# Revit family: FP-Revit20-en-CG301DNGGB5-CG301DNGGG5-GasCooktop-xxxxxxx-xx
name_source: partatom
category: Generic Models
units: mm (PartAtom-declared; Revit-internal decimal feet)

## family parameters
Always vertical = No
Can host rebar = No
Cut with Voids When Loaded = No
Part Type = Normal
Room Calculation Point = No
Round Connector Dimension = Use Diameter
Shared = No
Work Plane-Based = Yes

## types (2) — shared parameters
Chassis - Depth = 484 mm  [stored 1.58793 ft]
Chassis - Height = 61 mm  [stored 0.200131 ft]
Chassis - Width = 256 mm  [stored 0.839895 ft]
Clearance - Combustible = Fisher & Paykel - Clearance Required (Combustible)
Clearance - Non-Combustible = Fisher & Paykel - Clearance Required (Non-Combustible)
Clearance - Overhead Combustible = 650 mm  [stored 2.13255 ft]
Clearance - Overhead Exhaust Fan = 800 mm  [stored 2.62467 ft]
Clearance - Overhead Non-Combustible = 500 mm  [stored 1.64042 ft]
Clearance - Overhead Rangehood = Fisher & Paykel - Clearance Required (Rangehood)
Clearance - Rear Combustible = 85 mm  [stored 0.278871 ft]
Clearance - Side Combustible = 120 mm  [stored 0.393701 ft]
Default Elevation = 1219 mm
Description = Gas on Glass Modular Cooktop, 30cm
Manufacturer = Fisher & Paykel Appliances
Product - Depth = 530 mm  [stored 1.73885 ft]
Product - Height = 127 mm  [stored 0.416667 ft]
Product - Width = 300 mm  [stored 0.984252 ft]
URL = www.fisherpaykel.com

## per-type parameters (varying)
| type | Cooktop glass | Model |
| CG301DNGGB5 (Black) | Fisher & Paykel - Glass, Black | CG301DNGGB5 |
| CG301DNGGG5 (Grey) | Fisher & Paykel - Glass, Grey | CG301DNGGG5 |

note: [stored X ft] marks values corroborated as IEEE doubles in the binary element streams (Revit-internal decimal feet)

## geometry (parser evidence)
native form markers: Sweep x16
no freeform markers — native parametric forms only
